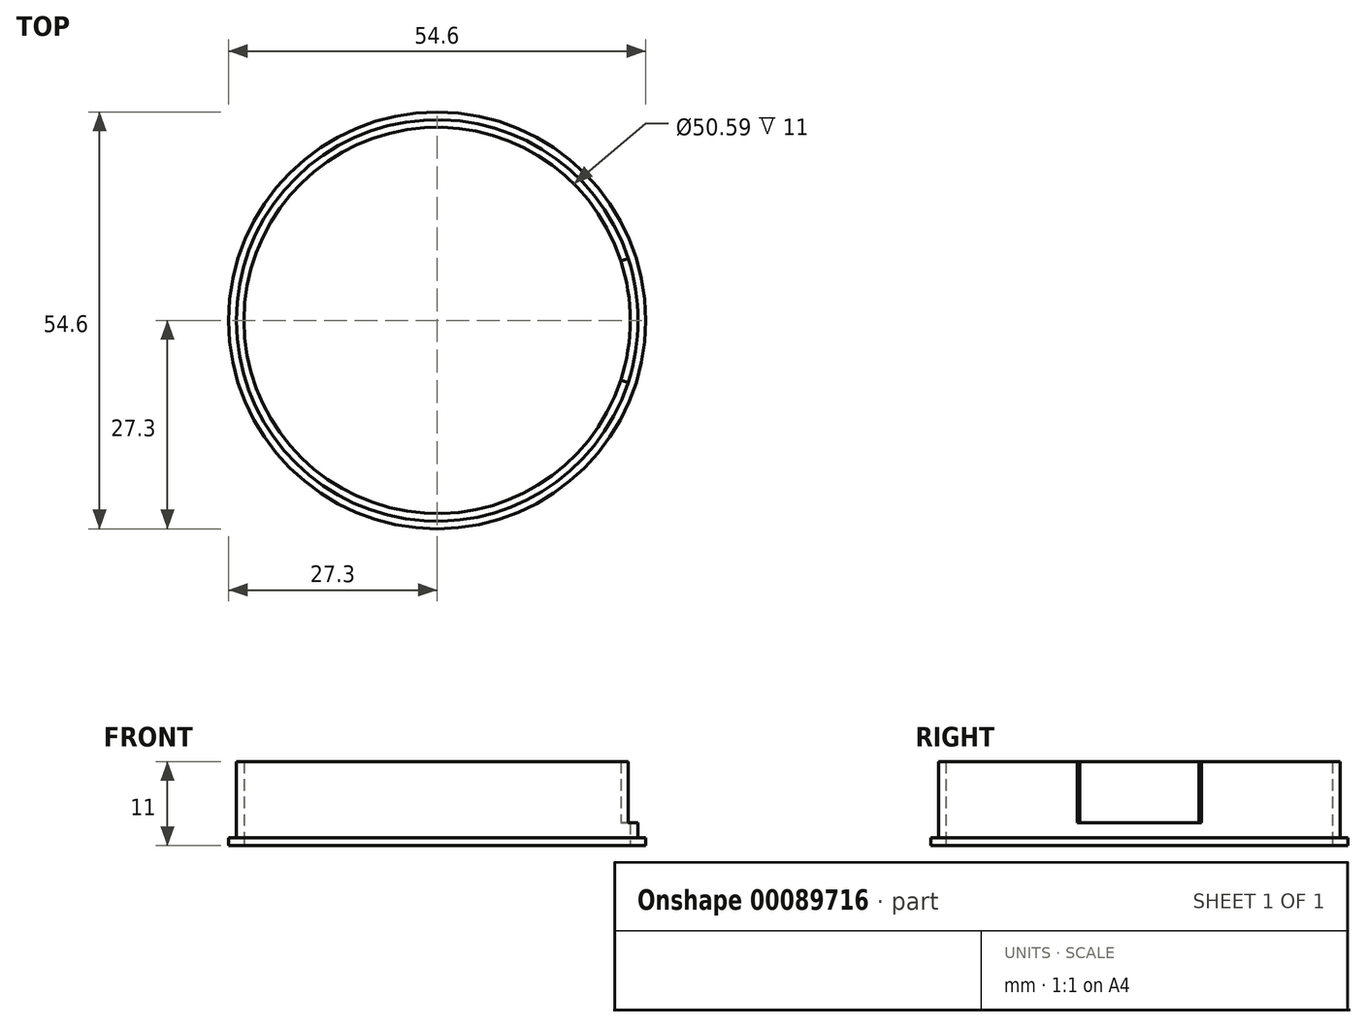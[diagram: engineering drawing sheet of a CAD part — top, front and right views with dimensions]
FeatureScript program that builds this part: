
annotation { "Feature Type Name" : "Feature", "Feature Type Description" : "" }
export const myFeature = defineFeature(function(context is Context, id is Id, definition is map)
    precondition{}
    {
        {
            var Q0;
            Q0=qCreatedBy(makeId("Front.planeOp"),FACE);
            var sketch = newSketch(context, id + "F0", { "sketchPlane" : qUnion([Q0])});
            skLineSegment(sketch, "E0", {"start": v(25.3, 0) * mm, "end": v(25.3, 11) * mm});
            skLineSegment(sketch, "E1", {"start": v(25.3, 11) * mm, "end": v(26.3, 11) * mm});
            skLineSegment(sketch, "E2", {"start": v(26.3, 11) * mm, "end": v(26.3, 1) * mm});
            skLineSegment(sketch, "E3", {"start": v(26.3, 1) * mm, "end": v(27.3, 1) * mm});
            skLineSegment(sketch, "E4", {"start": v(27.3, 1) * mm, "end": v(27.3, 0) * mm});
            skLineSegment(sketch, "E5", {"start": v(27.3, 0) * mm, "end": v(25.3, 0) * mm});
            skPoint(sketch, "E6", {"position": v(0, 0) * mm});
            skLineSegment(sketch, "E7", {"start": v(0, 0) * mm, "end": v(0, 17.76) * mm});
            skLineSegment(sketch, "E8.bottom", {"start": v(28.27, 12.98) * mm, "end": v(17.5, 12.98) * mm});
            skLineSegment(sketch, "E8.top", {"start": v(28.27, 2.98) * mm, "end": v(17.5, 2.98) * mm});
            skLineSegment(sketch, "E8.left", {"start": v(28.27, 12.98) * mm, "end": v(28.27, 2.98) * mm});
            skLineSegment(sketch, "E8.right", {"start": v(17.5, 12.98) * mm, "end": v(17.5, 2.98) * mm});
            skPoint(sketch, "E8.middle", {"position": v(22.89, 7.98) * mm});
            skSolve(sketch);
        }
        {
            var Q0;
            {var subQ0=sQuery(id+"F0.wireOp",EDGE,"E3");Q0=makeQuery(id+"F0.imprint","IMPRINT",FACE,{"disambiguationData":[TD([[makeQuery(id+"F0.imprint","IMPRINT",EDGE,{"derivedFrom":subQ0}),-1.0]])]});}
            var Q1;
            {var subQ0=sQuery(id+"F0.wireOp",EDGE,"E8.top");var subQ1=sQuery(id+"F0.wireOp",EDGE,"E0");var subQ2=makeQuery(id+"F0.imprint","INTERSECT",VERTEX,{"derivedFrom":[subQ1,subQ0]});Q1=makeQuery(id+"F0.imprint","IMPRINT",FACE,{"disambiguationData":[TD([[makeQuery(id+"F0.imprint","IMPRINT",EDGE,{"disambiguationData":[TD([[subQ2,-1.0]])],"derivedFrom":subQ1}),-1.0]])]});}
            var Q2;
            Q2=sQuery(id+"F0.wireOp",EDGE,"E7");
            revolve(context, id + "F1", {"entities" : qUnion([Q0, Q1]), "axis" : qUnion([Q2]), "revolveType" : RevolveType.FULL});
        }
        {
            var Q0;
            {var subQ5=sQuery(id+"F0.wireOp",EDGE,"E8.left");Q0=makeQuery(id+"F0.imprint","IMPRINT",FACE,{"disambiguationData":[TD([[makeQuery(id+"F0.imprint","IMPRINT",EDGE,{"derivedFrom":subQ5}),-1.0]])]});}
            var Q1;
            {var subQ0=sQuery(id+"F0.wireOp",EDGE,"E8.top");var subQ1=sQuery(id+"F0.wireOp",EDGE,"E0");var subQ2=makeQuery(id+"F0.imprint","INTERSECT",VERTEX,{"derivedFrom":[subQ1,subQ0]});Q1=makeQuery(id+"F0.imprint","IMPRINT",FACE,{"disambiguationData":[TD([[makeQuery(id+"F0.imprint","IMPRINT",EDGE,{"disambiguationData":[TD([[subQ2,-1.0]])],"derivedFrom":subQ1}),-1.0]])]});}
            var Q2;
            Q2=sQuery(id+"F0.wireOp",EDGE,"E7");
            revolve(context, id + "F2", {"operationType" : NewBodyOperationType.REMOVE, "entities" : qUnion([Q0, Q1]), "axis" : qUnion([Q2]), "revolveType" : RevolveType.SYMMETRIC, "angle" : 36 * degree});
        }
    });
